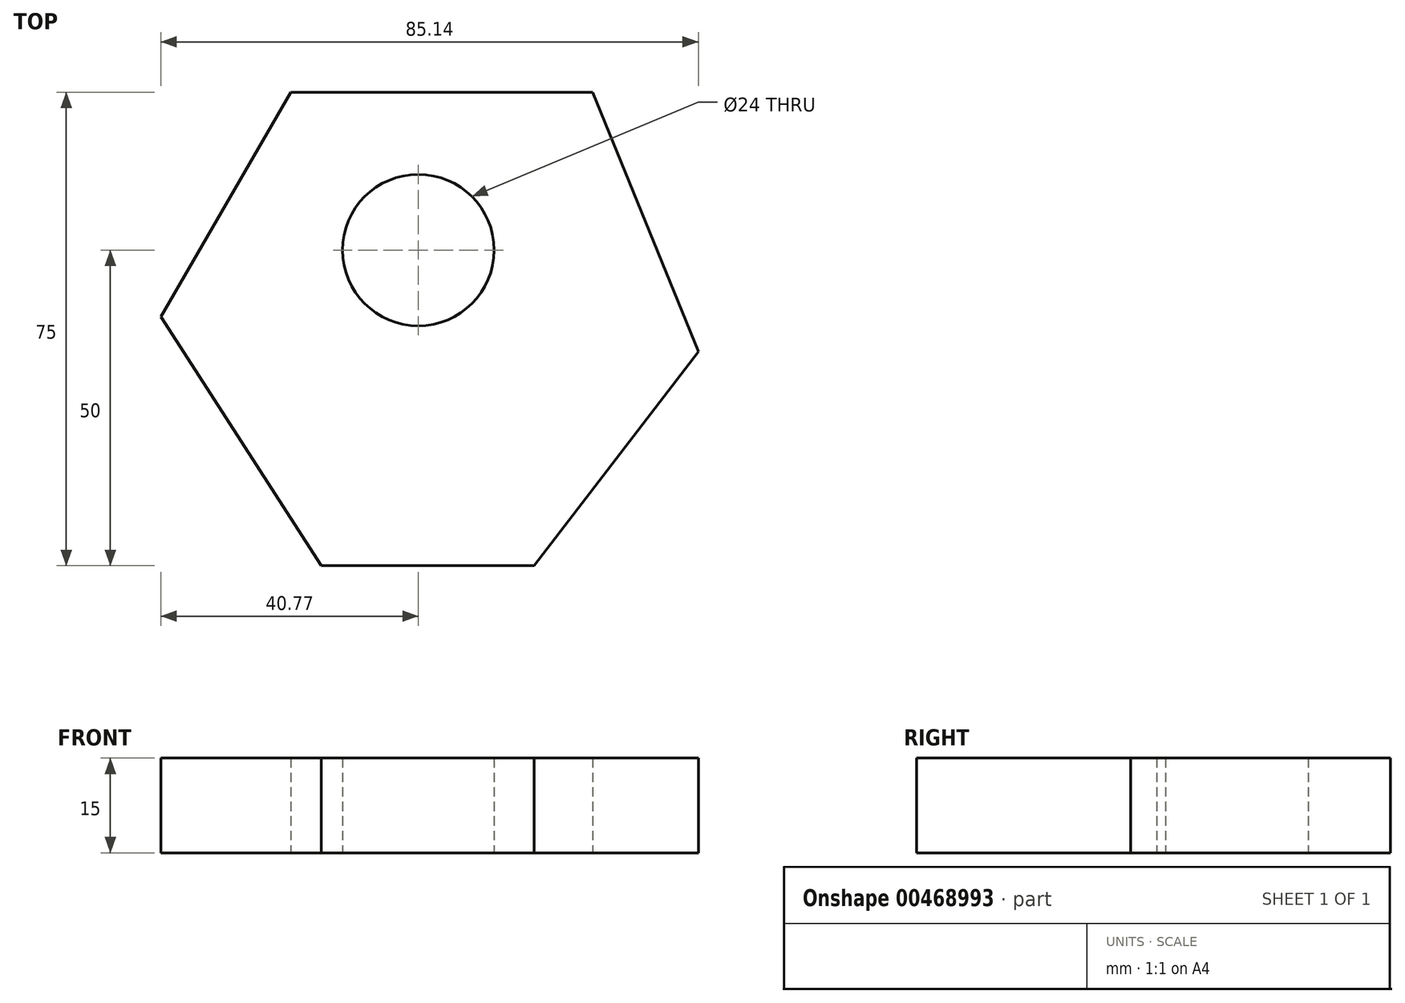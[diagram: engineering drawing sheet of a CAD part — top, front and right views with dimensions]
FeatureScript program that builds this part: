
annotation { "Feature Type Name" : "Feature", "Feature Type Description" : "" }
export const myFeature = defineFeature(function(context is Context, id is Id, definition is map)
    precondition{}
    {
        {
            var Q0;
            Q0=qCreatedBy(makeId("Top.planeOp"),FACE);
            var sketch = newSketch(context, id + "F0", { "sketchPlane" : qUnion([Q0])});
            skCircle(sketch, "E0", {"center": v(0, 0) * mm, "radius": 12 * mm});
            skLineSegment(sketch, "E1", {"start": v(-20.2, 25) * mm, "end": v(27.6, 25) * mm});
            skLineSegment(sketch, "E2", {"start": v(-20.2, 25) * mm, "end": v(-40.77, -10.59) * mm});
            skLineSegment(sketch, "E3", {"start": v(27.6, 25) * mm, "end": v(44.37, -16.1) * mm});
            skLineSegment(sketch, "E4", {"start": v(-40.77, -10.59) * mm, "end": v(-15.36, -50) * mm});
            skLineSegment(sketch, "E5", {"start": v(44.37, -16.1) * mm, "end": v(18.34, -50) * mm});
            skLineSegment(sketch, "E6", {"start": v(-15.36, -50) * mm, "end": v(18.34, -50) * mm});
            skLineSegment(sketch, "E7", {"start": v(0, 0) * mm, "end": v(-25.97, 15.01) * mm, "construction": true});
            skLineSegment(sketch, "E8", {"start": v(0, 0) * mm, "end": v(-33.62, -21.67) * mm, "construction": true});
            skLineSegment(sketch, "E9", {"start": v(0, 0) * mm, "end": v(0, -50) * mm, "construction": true});
            skLineSegment(sketch, "E10", {"start": v(0, 0) * mm, "end": v(35.69, -27.41) * mm, "construction": true});
            skLineSegment(sketch, "E11", {"start": v(0, 0) * mm, "end": v(32.4, 13.22) * mm, "construction": true});
            skLineSegment(sketch, "E12", {"start": v(0, 0) * mm, "end": v(0, 25) * mm, "construction": true});
            skSolve(sketch);
        }
        {
            var Q0;
            Q0=makeQuery(id+"F0.imprint","IMPRINT",FACE,{"disambiguationData":[TD([[makeQuery(id+"F0.imprint","IMPRINT",EDGE,{"derivedFrom":sQuery(id+"F0.wireOp",EDGE,"E0")}),-1.0]])]});
            extrude(context, id + "F1", {"entities" : qUnion([Q0]), "depth" : 15 * mm});
        }
    });
